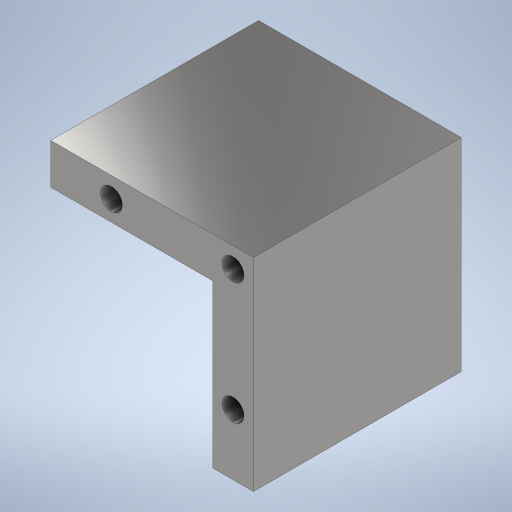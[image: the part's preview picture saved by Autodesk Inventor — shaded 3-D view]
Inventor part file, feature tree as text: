
AUTODESK INVENTOR PART (.ipt)
format: ipt  version: 2023 (Build 270158000, 158)  size: 229,376 bytes
history: native  units: mm
features: sketch x2, extrude x1, hole x1
ambient origin geometry x8: Origin, YZ Plane, XZ Plane, XY Plane, X Axis, Y Axis, Z Axis, Center Point
bodies: Solid1 (feature_tree)
feature tree (4):
  extrude  "Extrusion1"  Depth=40.0mm
  hole  "Hole1"  [1 undecoded]
  sketch  "Sketch1"  dims[d0=40.0mm d1=40.0mm]
  sketch  "Sketch2"  dims[d3=8.0mm d4=41.0mm d5=0.0mm d6=4.0mm d7=4.0mm d8=24.0mm d9=24.0mm d10=4.3mm d11=6.0mm d12=4.0mm d13=2.0mm d14=90.0deg d15=5.0mm d16=20.594885mm]
note: 1 required parameter value undecoded (feature->parameter linkage not recoverable at this tier; creation-order binding heuristic only, values carry confidence <= 0.55)
